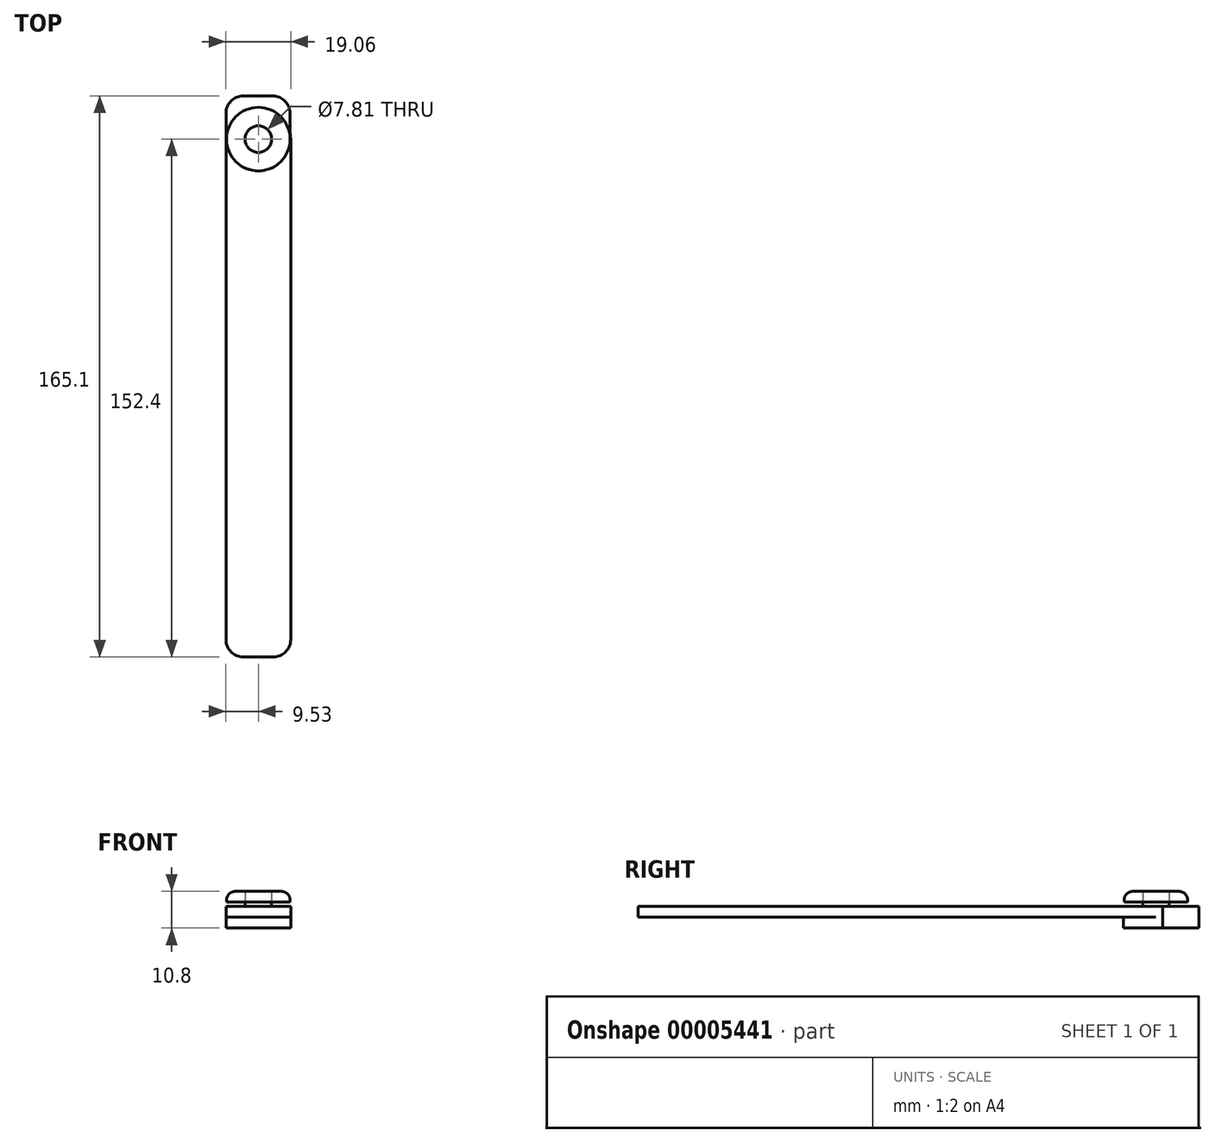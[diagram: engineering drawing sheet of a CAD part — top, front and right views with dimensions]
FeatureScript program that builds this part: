
annotation { "Feature Type Name" : "Feature", "Feature Type Description" : "" }
export const myFeature = defineFeature(function(context is Context, id is Id, definition is map)
    precondition{}
    {
        {
            var Q0;
            Q0=qCreatedBy(makeId("Top.planeOp"),FACE);
            var sketch = newSketch(context, id + "F0", { "sketchPlane" : qUnion([Q0])});
            skArc(sketch, "E0", {"start": v(-9.53, 0) * mm, "mid": v(0.98, -9.47) * mm, "end": v(9.32, 1.94) * mm});
            skLineSegment(sketch, "E1.top", {"start": v(-9.53, 12.7) * mm, "end": v(9.32, 12.7) * mm});
            skLineSegment(sketch, "E1.left", {"start": v(-9.53, 0) * mm, "end": v(-9.53, 12.7) * mm});
            skLineSegment(sketch, "E1.right", {"start": v(9.32, 0) * mm, "end": v(9.32, 12.7) * mm});
            skSolve(sketch);
        }
        {
            var Q0;
            {var subQ2=sQuery(id+"F0.wireOp",EDGE,"E0");Q0=makeQuery(id+"F0.imprint","IMPRINT",FACE,{"disambiguationData":[TD([[makeQuery(id+"F0.imprint","IMPRINT",EDGE,{"derivedFrom":subQ2}),1.0]])]});}
            extrude(context, id + "F1", {"entities" : qUnion([Q0]), "depth" : 3.17 * mm});
        }
        {
            var Q0;
            Q0=makeQuery(id+"F1.opExtrude","CAP_FACE",FACE,{"disambiguationData":[OSD([sQuery(id+"F0.wireOp",EDGE,"E0"),sQuery(id+"F0.wireOp",EDGE,"E1.top"),sQuery(id+"F0.wireOp",EDGE,"E1.left"),sQuery(id+"F0.wireOp",EDGE,"E1.right")])],"isStart":false});
            var sketch = newSketch(context, id + "F2", { "sketchPlane" : qUnion([Q0])});
            skLineSegment(sketch, "E2.bottom", {"start": v(-9.53, 12.7) * mm, "end": v(9.53, 12.7) * mm});
            skLineSegment(sketch, "E2.top", {"start": v(-9.53, 0) * mm, "end": v(9.53, 0) * mm});
            skLineSegment(sketch, "E2.left", {"start": v(-9.53, 12.7) * mm, "end": v(-9.53, 0) * mm});
            skLineSegment(sketch, "E2.right", {"start": v(9.53, 12.7) * mm, "end": v(9.53, 0) * mm});
            skSolve(sketch);
        }
        {
            var Q0;
            {var subQ1=sQuery(id+"F2.wireOp",EDGE,"E2.top");Q0=makeQuery(id+"F2.imprint","IMPRINT",FACE,{"disambiguationData":[TD([[makeQuery(id+"F2.imprint","IMPRINT",EDGE,{"derivedFrom":subQ1}),1.0]])]});}
            extrude(context, id + "F3", {"entities" : qUnion([Q0]), "operationType" : NewBodyOperationType.ADD, "depth" : 3.17 * mm});
        }
        {
            var Q0;
            Q0=makeQuery(id+"F3.opExtrude","SWEPT_FACE",FACE,{"disambiguationData":[OSD([sQuery(id+"F2.wireOp",EDGE,"E2.top")])]});
            extrude(context, id + "F4", {"entities" : qUnion([Q0]), "operationType" : NewBodyOperationType.ADD, "depth" : 152.4 * mm});
        }
        {
            var Q0;
            Q0=makeQuery(id+"F1.opExtrude","CAP_FACE",FACE,{"disambiguationData":[OSD([sQuery(id+"F0.wireOp",EDGE,"E0"),sQuery(id+"F0.wireOp",EDGE,"E1.top"),sQuery(id+"F0.wireOp",EDGE,"E1.left"),sQuery(id+"F0.wireOp",EDGE,"E1.right")])],"isStart":true});
            var sketch = newSketch(context, id + "F5", { "sketchPlane" : qUnion([Q0])});
            skCircle(sketch, "E3", {"center": v(0, 0) * mm, "radius": 3.9 * mm});
            skSolve(sketch);
        }
        {
            var Q0;
            Q0=makeQuery(id+"F5.imprint","IMPRINT",FACE,{"disambiguationData":[TD([[makeQuery(id+"F5.imprint","IMPRINT",EDGE,{"derivedFrom":sQuery(id+"F5.wireOp",EDGE,"E3")}),1.0]])]});
            extrude(context, id + "F6", {"entities" : qUnion([Q0]), "operationType" : NewBodyOperationType.ADD, "oppositeDirection" : true, "depth" : 7.62 * mm});
        }
        {
            var Q0;
            Q0=makeQuery(id+"F6.opExtrude","CAP_FACE",FACE,{"disambiguationData":[OSD([sQuery(id+"F5.wireOp",EDGE,"E3")])],"isStart":false});
            var sketch = newSketch(context, id + "F7", { "sketchPlane" : qUnion([Q0])});
            skCircle(sketch, "E4", {"center": v(0, 0) * mm, "radius": 9.36 * mm});
            skSolve(sketch);
        }
        {
            var Q0;
            Q0=makeQuery(id+"F7.imprint","IMPRINT",FACE,{"disambiguationData":[TD([[makeQuery(id+"F7.imprint","IMPRINT",EDGE,{"derivedFrom":sQuery(id+"F7.wireOp",EDGE,"E4")}),1.0]])]});
            extrude(context, id + "F8", {"entities" : qUnion([Q0]), "depth" : 3.17 * mm});
        }
        {
            var Q0;
            Q0=makeQuery(id+"F4.opExtrude","CAP_EDGE",EDGE,{"disambiguationData":[OSD([sQuery(id+"F0.wireOp",EDGE,"E0"),sQuery(id+"F2.wireOp",EDGE,"E2.top"),sQuery(id+"F2.wireOp",EDGE,"E2.left")])],"isStart":false});
            var Q1;
            Q1=makeQuery(id+"F4.opExtrude","CAP_EDGE",EDGE,{"disambiguationData":[OSD([sQuery(id+"F0.wireOp",EDGE,"E0"),sQuery(id+"F2.wireOp",EDGE,"E2.top"),sQuery(id+"F2.wireOp",EDGE,"E2.right")])],"isStart":false});
            var Q2;
            Q2=makeQuery(id+"F3.boolean.opBoolean","MERGE",EDGE,{"derivedFrom":[makeQuery(id+"F1.opExtrude","SWEPT_EDGE",EDGE,{"disambiguationData":[OSD([sQuery(id+"F0.wireOp",EDGE,"E1.top"),sQuery(id+"F0.wireOp",EDGE,"E1.left")])]}),makeQuery(id+"F3.opExtrude","SWEPT_EDGE",EDGE,{"disambiguationData":[OSD([sQuery(id+"F2.wireOp",EDGE,"E2.bottom"),sQuery(id+"F2.wireOp",EDGE,"E2.left")])]})]});
            var Q3;
            {var subQ0=sQuery(id+"F0.wireOp",EDGE,"E1.right");Q3=makeQuery(id+"F3.boolean.opBoolean","MERGE",EDGE,{"derivedFrom":[makeQuery(id+"F1.opExtrude","SWEPT_EDGE",EDGE,{"disambiguationData":[OSD([sQuery(id+"F0.wireOp",EDGE,"E1.top"),subQ0])]}),makeQuery(id+"F3.opExtrude","SWEPT_EDGE",EDGE,{"disambiguationData":[OSD([subQ0,sQuery(id+"F2.wireOp",EDGE,"E2.bottom")])]})]});}
            fillet(context, id + "F9", {"entities" : qUnion([Q0, Q1, Q2, Q3]), "radius" : 5.08 * mm, "tangentPropagation" : true, "allowEdgeOverflow" : false});
        }
        {
            var Q0;
            Q0=makeQuery(id+"F8.opExtrude","CAP_EDGE",EDGE,{"disambiguationData":[OSD([sQuery(id+"F7.wireOp",EDGE,"E4")])],"isStart":false});
            fillet(context, id + "F10", {"entities" : qUnion([Q0]), "radius" : 2.54 * mm, "tangentPropagation" : true, "allowEdgeOverflow" : false});
        }
    });
